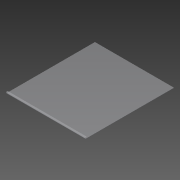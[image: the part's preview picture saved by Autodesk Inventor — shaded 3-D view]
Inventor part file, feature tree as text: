
AUTODESK INVENTOR PART (.ipt)
format: ipt  version: 2013 (Build 170138000, 138)  size: 101,376 bytes
history: native  units: in
note: dims shown in document units (in); Inventor stores cm internally (conversion verified against a paired STEP export)
features: sheet_metal_op x7, sketch x3, other x3
ambient origin geometry x8: Origin, YZ Plane, XZ Plane, XY Plane, X Axis, Y Axis, Z Axis, Center Point
bodies: Solid1 (feature_tree)
feature tree (13):
  sheet_metal_op  "Face1"
  sheet_metal_op  "Flange1"
  sheet_metal_op  "Flange2"
  sketch  "Sketch1"  dims[d0=48.0in]
  other  "Plate1"
  sketch  "Sketch2"  dims[d1=54.0in]
  other  "Plate2"
  sheet_metal_op  "Bend1"
  sheet_metal_op  "Corner1"
  sketch  "Sketch3"  dims[d2=0.2125in d3=0.2125in d4=0.1063in d5=0.425in d6=0.2125in d7=1.0in d8=90.0deg d9=0.2125in d10=0.85in d11=0.2125in d12=0.2125in d13=0.2125in d14=0.1063in d15=0.425in d16=0.2125in d17=1.0in d18=90.0deg d19=0.2125in d20=0.85in d21=0.2125in d22=0.2125in]
  other  "Plate3"
  sheet_metal_op  "Bend2"
  sheet_metal_op  "Corner2"
